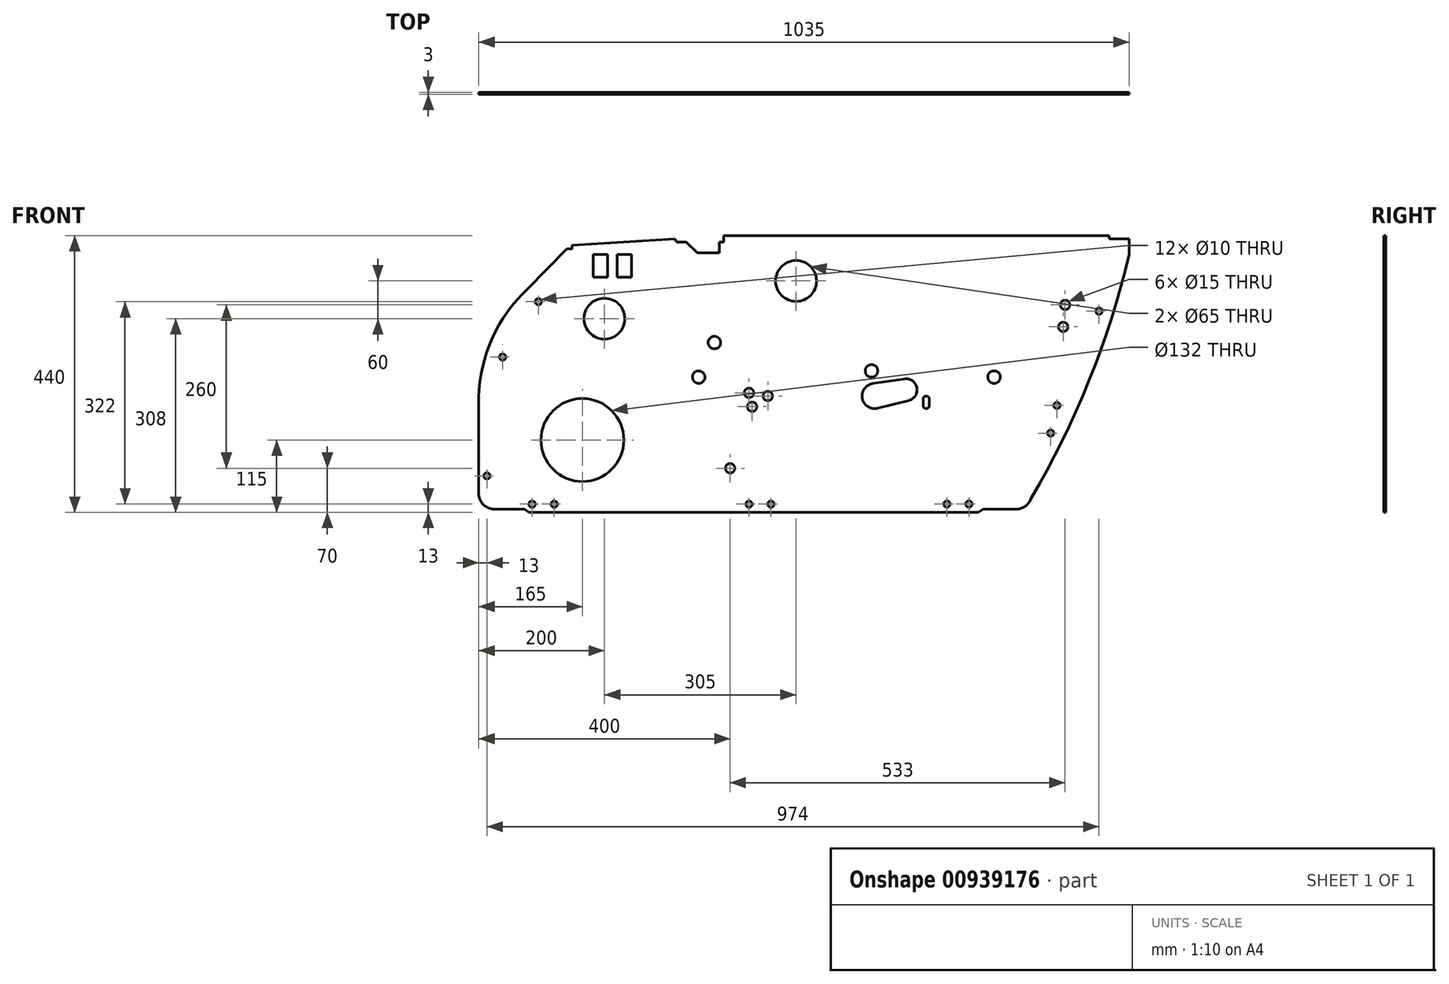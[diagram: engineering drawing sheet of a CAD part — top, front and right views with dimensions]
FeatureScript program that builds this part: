
annotation { "Feature Type Name" : "Feature", "Feature Type Description" : "" }
export const myFeature = defineFeature(function(context is Context, id is Id, definition is map)
    precondition{}
    {
        {
            var Q0;
            Q0=qCreatedBy(makeId("Front.planeOp"),FACE);
            var sketch = newSketch(context, id + "F0", { "sketchPlane" : qUnion([Q0])});
            skLineSegment(sketch, "E0.bottom", {"start": v(-127.5, 220) * mm, "end": v(485.5, 220) * mm});
            skLineSegment(sketch, "E0.top", {"start": v(-437.5, -220) * mm, "end": v(277.5, -220) * mm});
            skLineSegment(sketch, "E0.left", {"start": v(-517.5, -36.86) * mm, "end": v(-517.5, -190) * mm});
            skLineSegment(sketch, "E0.right", {"start": v(517.5, 215) * mm, "end": v(517.5, 190) * mm});
            skPoint(sketch, "E1", {"position": v(-127.5, 220) * mm});
            skLineSegment(sketch, "E2", {"start": v(-369.3, 204.5) * mm, "end": v(-205.02, 215.03) * mm});
            skLineSegment(sketch, "E3", {"start": v(-439.92, 135) * mm, "end": v(-377.6, 199.28) * mm});
            skPoint(sketch, "E4", {"position": v(517.5, 190) * mm});
            skPoint(sketch, "E5", {"position": v(-352.5, -105) * mm});
            skCircle(sketch, "E6", {"center": v(-352.5, -105) * mm, "radius": 66 * mm});
            skPoint(sketch, "E7", {"position": v(-317.5, 88) * mm});
            skCircle(sketch, "E8", {"center": v(-317.5, 88) * mm, "radius": 32.5 * mm});
            skPoint(sketch, "E9", {"position": v(-127.5, 210) * mm});
            skPoint(sketch, "E10", {"position": v(-134.75, 210) * mm});
            skPoint(sketch, "E11", {"position": v(-134.75, 192.47) * mm});
            skPoint(sketch, "E12", {"position": v(-169.75, 192.47) * mm});
            skPoint(sketch, "E13", {"position": v(-187.5, 210) * mm});
            skPoint(sketch, "E14", {"position": v(-202.5, 210) * mm});
            skLineSegment(sketch, "E15", {"start": v(-202.5, 210) * mm, "end": v(-205.02, 215.03) * mm});
            skLineSegment(sketch, "E16", {"start": v(-202.5, 210) * mm, "end": v(-187.5, 210) * mm});
            skLineSegment(sketch, "E17", {"start": v(-187.5, 210) * mm, "end": v(-169.75, 192.47) * mm});
            skLineSegment(sketch, "E18", {"start": v(-169.75, 192.47) * mm, "end": v(-134.75, 192.47) * mm});
            skLineSegment(sketch, "E19", {"start": v(-134.75, 192.47) * mm, "end": v(-134.75, 210) * mm});
            skLineSegment(sketch, "E20", {"start": v(-134.75, 210) * mm, "end": v(-127.5, 210) * mm});
            skLineSegment(sketch, "E21", {"start": v(-127.5, 210) * mm, "end": v(-127.5, 220) * mm});
            skPoint(sketch, "E22", {"position": v(-274.5, 190) * mm});
            skPoint(sketch, "E23", {"position": v(-297.5, 190) * mm});
            skPoint(sketch, "E24", {"position": v(-312.5, 190) * mm});
            skPoint(sketch, "E25", {"position": v(-335.5, 190) * mm});
            skPoint(sketch, "E26", {"position": v(-274.5, 154) * mm});
            skPoint(sketch, "E27", {"position": v(-312.5, 154) * mm});
            skLineSegment(sketch, "E28.bottom", {"start": v(-312.5, 154) * mm, "end": v(-335.5, 154) * mm});
            skLineSegment(sketch, "E28.top", {"start": v(-312.5, 190) * mm, "end": v(-335.5, 190) * mm});
            skLineSegment(sketch, "E28.left", {"start": v(-312.5, 154) * mm, "end": v(-312.5, 190) * mm});
            skLineSegment(sketch, "E28.right", {"start": v(-335.5, 154) * mm, "end": v(-335.5, 190) * mm});
            skLineSegment(sketch, "E29.bottom", {"start": v(-274.5, 154) * mm, "end": v(-297.5, 154) * mm});
            skLineSegment(sketch, "E29.top", {"start": v(-274.5, 190) * mm, "end": v(-297.5, 190) * mm});
            skLineSegment(sketch, "E29.left", {"start": v(-274.5, 154) * mm, "end": v(-274.5, 190) * mm});
            skLineSegment(sketch, "E29.right", {"start": v(-297.5, 154) * mm, "end": v(-297.5, 190) * mm});
            skPoint(sketch, "E30", {"position": v(-12.5, 148) * mm});
            skCircle(sketch, "E31", {"center": v(-12.5, 148) * mm, "radius": 32.5 * mm});
            skCircle(sketch, "E32", {"center": v(302.5, -5) * mm, "radius": 10 * mm});
            skArc(sketch, "E33", {"start": v(109.54, -15.22) * mm, "mid": v(92.89, -38.92) * mm, "end": v(117.38, -54.4) * mm});
            skArc(sketch, "E34", {"start": v(166.77, -41.97) * mm, "mid": v(179.66, -21.57) * mm, "end": v(159.91, -7.7) * mm});
            skLineSegment(sketch, "E35", {"start": v(109.54, -15.22) * mm, "end": v(159.91, -7.7) * mm});
            skLineSegment(sketch, "E36", {"start": v(117.38, -54.4) * mm, "end": v(166.77, -41.97) * mm});
            skCircle(sketch, "E37", {"center": v(107.5, 5) * mm, "radius": 10 * mm});
            skCircle(sketch, "E38", {"center": v(415.5, 110) * mm, "radius": 7.5 * mm});
            skCircle(sketch, "E39", {"center": v(412.5, 75) * mm, "radius": 7.5 * mm});
            skCircle(sketch, "E40", {"center": v(-142.5, 50) * mm, "radius": 10 * mm});
            skCircle(sketch, "E41", {"center": v(-167.5, -5) * mm, "radius": 10 * mm});
            skCircle(sketch, "E42", {"center": v(-432.5, -207) * mm, "radius": 5 * mm});
            skCircle(sketch, "E43", {"center": v(-397.5, -207) * mm, "radius": 5 * mm});
            skCircle(sketch, "E44", {"center": v(262.5, -206.81) * mm, "radius": 5 * mm});
            skCircle(sketch, "E45", {"center": v(227.5, -206.81) * mm, "radius": 5 * mm});
            skCircle(sketch, "E46", {"center": v(-52.5, -207) * mm, "radius": 5 * mm});
            skCircle(sketch, "E47", {"center": v(-87.5, -207) * mm, "radius": 5 * mm});
            skPoint(sketch, "E48", {"position": v(-437.5, -220) * mm});
            skLineSegment(sketch, "E49", {"start": v(-437.5, -220) * mm, "end": v(-444.28, -215) * mm});
            skLineSegment(sketch, "E50", {"start": v(-492.5, -215) * mm, "end": v(-444.28, -215) * mm});
            skPoint(sketch, "E51", {"position": v(277.5, -220) * mm});
            skLineSegment(sketch, "E52.top", {"start": v(285, -215) * mm, "end": v(337.62, -215) * mm});
            skLineSegment(sketch, "E53", {"start": v(277.5, -220) * mm, "end": v(285, -215) * mm});
            skPoint(sketch, "E54", {"position": v(485.5, 215) * mm});
            skLineSegment(sketch, "E55.bottom", {"start": v(485.5, 215) * mm, "end": v(517.5, 215) * mm});
            skLineSegment(sketch, "E55.left", {"start": v(485.5, 215) * mm, "end": v(485.5, 220) * mm});
            skPoint(sketch, "E56", {"position": v(-369.3, 199.28) * mm});
            skLineSegment(sketch, "E57.bottom", {"start": v(-369.3, 199.28) * mm, "end": v(-377.6, 199.28) * mm});
            skLineSegment(sketch, "E57.left", {"start": v(-369.3, 199.28) * mm, "end": v(-369.3, 204.5) * mm});
            skCircle(sketch, "E58", {"center": v(-87.5, -30) * mm, "radius": 7.5 * mm});
            skCircle(sketch, "E59", {"center": v(-57.5, -35) * mm, "radius": 7.5 * mm});
            skCircle(sketch, "E60", {"center": v(-82.5, -52) * mm, "radius": 7.5 * mm});
            skCircle(sketch, "E61", {"center": v(-504.5, -162) * mm, "radius": 5 * mm});
            skCircle(sketch, "E62", {"center": v(-479.5, 27) * mm, "radius": 5 * mm});
            skCircle(sketch, "E63", {"center": v(-422.5, 115) * mm, "radius": 5 * mm});
            skCircle(sketch, "E64", {"center": v(392.5, -94) * mm, "radius": 5 * mm});
            skCircle(sketch, "E65", {"center": v(402.5, -50) * mm, "radius": 5 * mm});
            skCircle(sketch, "E66", {"center": v(469.5, 100) * mm, "radius": 5 * mm});
            skArc(sketch, "E67", {"start": v(199.5, -40) * mm, "mid": v(194.5, -35) * mm, "end": v(189.5, -40) * mm});
            skArc(sketch, "E68", {"start": v(189.5, -50) * mm, "mid": v(194.5, -55) * mm, "end": v(199.5, -50) * mm});
            skLineSegment(sketch, "E69", {"start": v(189.5, -40) * mm, "end": v(189.5, -50) * mm});
            skLineSegment(sketch, "E70", {"start": v(199.5, -40) * mm, "end": v(199.5, -50) * mm});
            skArc(sketch, "E71", {"start": v(-439.92, 135) * mm, "mid": v(-495.98, 56.86) * mm, "end": v(-517.5, -36.86) * mm});
            skPoint(sketch, "E72", {"position": v(-492.5, -190) * mm});
            skArc(sketch, "E73", {"start": v(-517.5, -190) * mm, "mid": v(-510.18, -207.68) * mm, "end": v(-492.5, -215) * mm});
            skArc(sketch, "E74", {"start": v(337.62, -215) * mm, "mid": v(351.62, -210.72) * mm, "end": v(360.82, -199.33) * mm});
            skCircle(sketch, "E75", {"center": v(-117.5, -150) * mm, "radius": 7.5 * mm});
            skArc(sketch, "E76", {"start": v(360.82, -199.33) * mm, "mid": v(453.62, -10.49) * mm, "end": v(517.5, 190) * mm});
            skSolve(sketch);
        }
        {
            var Q0;
            Q0 = qSketchRegion(id + "F0", true);
            extrude(context, id + "F1", {"entities" : qUnion([Q0]), "depth" : 3 * mm, "offsetDistance" : 25 * mm});
        }
    });
